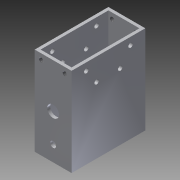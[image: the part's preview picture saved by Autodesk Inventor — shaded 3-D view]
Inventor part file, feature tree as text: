
AUTODESK INVENTOR PART (.ipt)
format: ipt  version: 2013 (Build 170138000, 138)  size: 184,832 bytes
history: native  units: mm
features: sketch x7, hole x5, thread x4, extrude x2, other x1
ambient origin geometry x1: Origin
feature tree (19):
  other  "ソリッド1"
  extrude  "押し出し1"  Depth=25.0mm
  extrude  "押し出し2"  Depth=50.0mm
  hole  "穴1"  [1 undecoded]
  hole  "穴2"  [1 undecoded]
  hole  "穴4"  [1 undecoded]
  thread  "ねじ1"
  thread  "ねじ2"
  thread  "ねじ3"
  thread  "ねじ4"
  hole  "穴5"  [1 undecoded]
  hole  "穴7"  [1 undecoded]
  sketch  "スケッチ1"
  sketch  "スケッチ2"
  sketch  "スケッチ3"
  sketch  "スケッチ4"
  sketch  "スケッチ5"
  sketch  "スケッチ7"
  sketch  "スケッチ8"
note: 5 required parameter values undecoded (feature->parameter linkage not recoverable at this tier; creation-order binding heuristic only, values carry confidence <= 0.55)
